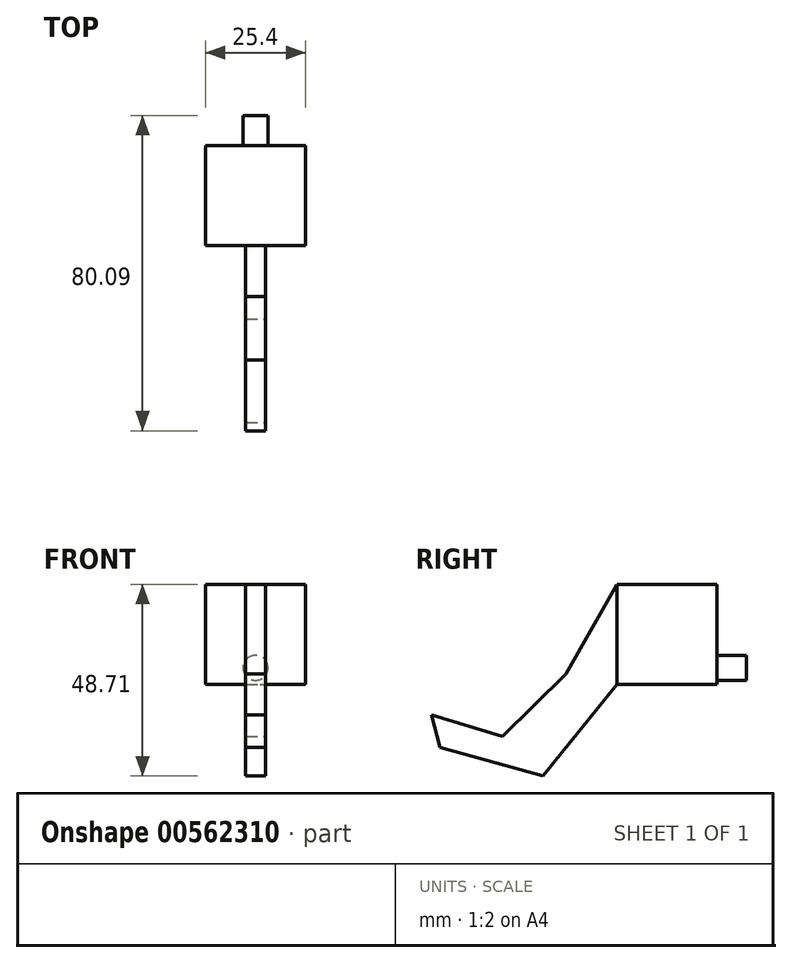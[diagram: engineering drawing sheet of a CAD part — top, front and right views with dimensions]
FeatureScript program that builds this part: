
annotation { "Feature Type Name" : "Feature", "Feature Type Description" : "" }
export const myFeature = defineFeature(function(context is Context, id is Id, definition is map)
    precondition{}
    {
        {
            var Q0;
            Q0=qCreatedBy(makeId("Top.planeOp"),FACE);
            var sketch = newSketch(context, id + "F0", { "sketchPlane" : qUnion([Q0])});
            skLineSegment(sketch, "E0.bottom", {"start": v(-12.7, 0) * mm, "end": v(12.7, 0) * mm});
            skLineSegment(sketch, "E0.top", {"start": v(-12.7, 25.4) * mm, "end": v(12.7, 25.4) * mm});
            skLineSegment(sketch, "E0.left", {"start": v(-12.7, 0) * mm, "end": v(-12.7, 25.4) * mm});
            skLineSegment(sketch, "E0.right", {"start": v(12.7, 0) * mm, "end": v(12.7, 25.4) * mm});
            skSolve(sketch);
        }
        {
            var Q0;
            Q0 = qSketchRegion(id + "F0", true);
            extrude(context, id + "F1", {"entities" : qUnion([Q0]), "depth" : 25.4 * mm, "offsetDistance" : 25.4 * mm});
        }
        {
            var Q0;
            Q0=qCreatedBy(makeId("Right.planeOp"),FACE);
            cPlane(context, id + "F2", {"entities" : qUnion([Q0]), "cplaneType" : CPlaneType.OFFSET, "offset" : 2.54 * mm, "width" : 152.4 * mm, "height" : 152.4 * mm});
        }
        {
            var Q0;
            Q0=qCreatedBy(id+"F2.planeOp",FACE);
            var sketch = newSketch(context, id + "F3", { "sketchPlane" : qUnion([Q0])});
            skLineSegment(sketch, "E1", {"start": v(0, 0) * mm, "end": v(-18.74, -23.31) * mm});
            skLineSegment(sketch, "E2", {"start": v(-18.74, -23.31) * mm, "end": v(-44.93, -16.07) * mm});
            skLineSegment(sketch, "E3", {"start": v(-44.93, -16.07) * mm, "end": v(-47.07, -7.83) * mm});
            skLineSegment(sketch, "E4", {"start": v(-12.92, 2.63) * mm, "end": v(0, 25.4) * mm});
            skLineSegment(sketch, "E5", {"start": v(0, 25.4) * mm, "end": v(0, 0) * mm});
            skLineSegment(sketch, "E6", {"start": v(-47.07, -7.83) * mm, "end": v(-29.09, -13.22) * mm});
            skLineSegment(sketch, "E7", {"start": v(-29.09, -13.22) * mm, "end": v(-12.92, 2.63) * mm});
            skSolve(sketch);
        }
        {
            var Q0;
            Q0 = qSketchRegion(id + "F3", true);
            extrude(context, id + "F4", {"entities" : qUnion([Q0]), "operationType" : NewBodyOperationType.ADD, "oppositeDirection" : true, "depth" : 5.08 * mm, "offsetDistance" : 25.4 * mm});
        }
        {
            var Q0;
            Q0=makeQuery(id+"F1.opExtrude","SWEPT_FACE",FACE,{"disambiguationData":[OSD([sQuery(id+"F0.wireOp",EDGE,"E0.top")])]});
            var sketch = newSketch(context, id + "F5", { "sketchPlane" : qUnion([Q0])});
            skCircle(sketch, "E8", {"center": v(0, 4.18) * mm, "radius": 3.17 * mm});
            skSolve(sketch);
        }
        {
            var Q0;
            Q0 = qSketchRegion(id + "F5", true);
            extrude(context, id + "F6", {"entities" : qUnion([Q0]), "operationType" : NewBodyOperationType.ADD, "depth" : 7.62 * mm, "offsetDistance" : 25.4 * mm});
        }
    });
